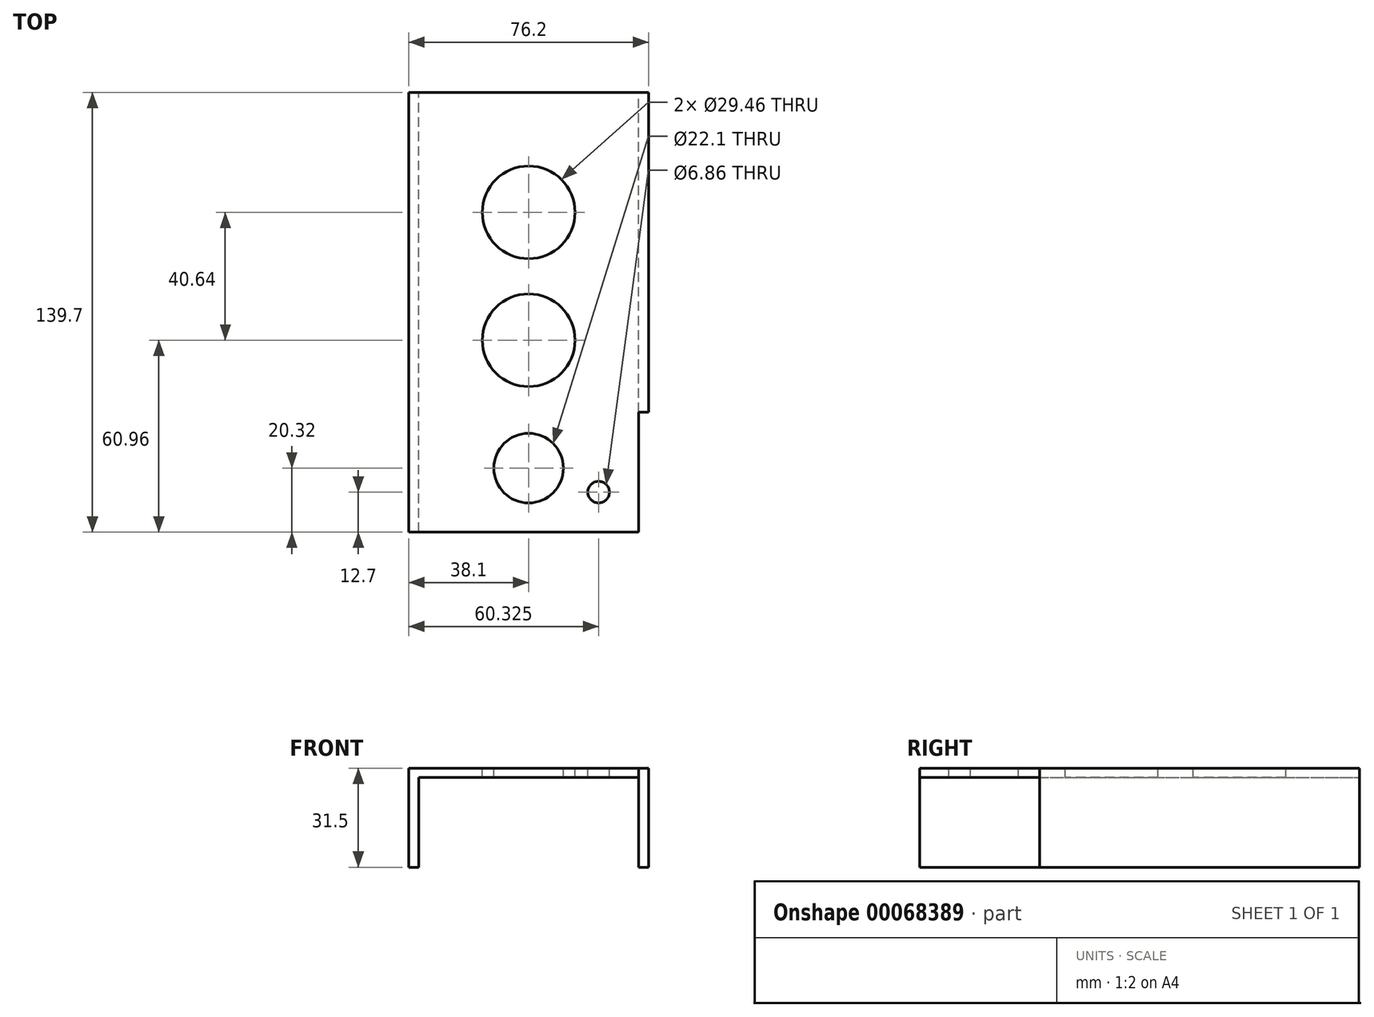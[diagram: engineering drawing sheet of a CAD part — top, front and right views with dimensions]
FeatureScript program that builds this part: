
annotation { "Feature Type Name" : "Feature", "Feature Type Description" : "" }
export const myFeature = defineFeature(function(context is Context, id is Id, definition is map)
    precondition{}
    {
        {
            var Q0;
            Q0=qCreatedBy(makeId("Top.planeOp"),FACE);
            var sketch = newSketch(context, id + "F0", { "sketchPlane" : qUnion([Q0])});
            skLineSegment(sketch, "E0.bottom", {"start": v(38.1, 69.85) * mm, "end": v(-38.1, 69.85) * mm});
            skLineSegment(sketch, "E0.top", {"start": v(38.1, -69.85) * mm, "end": v(-38.1, -69.85) * mm});
            skLineSegment(sketch, "E0.left", {"start": v(38.1, 69.85) * mm, "end": v(38.1, -69.85) * mm});
            skLineSegment(sketch, "E0.right", {"start": v(-38.1, 69.85) * mm, "end": v(-38.1, -69.85) * mm});
            skPoint(sketch, "E0.middle", {"position": v(0, 0) * mm});
            skSolve(sketch);
        }
        {
            var Q0;
            Q0 = qSketchRegion(id + "F0", true);
            extrude(context, id + "F1", {"entities" : qUnion([Q0]), "depth" : 4.76 * mm});
        }
        {
            var Q0;
            Q0=makeQuery(id+"F1.opExtrude","CAP_FACE",FACE,{"disambiguationData":[OSD([sQuery(id+"F0.wireOp",EDGE,"E0.bottom"),sQuery(id+"F0.wireOp",EDGE,"E0.top"),sQuery(id+"F0.wireOp",EDGE,"E0.left"),sQuery(id+"F0.wireOp",EDGE,"E0.right")])],"isStart":false});
            var sketch = newSketch(context, id + "F2", { "sketchPlane" : qUnion([Q0])});
            skLineSegment(sketch, "E1", {"start": v(0, -69.85) * mm, "end": v(34.92, -69.85) * mm, "construction": true});
            skLineSegment(sketch, "E2", {"start": v(0, -69.85) * mm, "end": v(-34.93, -69.85) * mm, "construction": true});
            skLineSegment(sketch, "E3.bottom", {"start": v(-34.93, -69.85) * mm, "end": v(-38.1, -69.85) * mm});
            skLineSegment(sketch, "E3.top", {"start": v(-34.93, 69.85) * mm, "end": v(-38.1, 69.85) * mm});
            skLineSegment(sketch, "E3.left", {"start": v(-34.93, -69.85) * mm, "end": v(-34.93, 69.85) * mm});
            skLineSegment(sketch, "E3.right", {"start": v(-38.1, -69.85) * mm, "end": v(-38.1, 69.85) * mm});
            skLineSegment(sketch, "E4.bottom", {"start": v(34.92, -69.85) * mm, "end": v(38.1, -69.85) * mm});
            skLineSegment(sketch, "E4.top", {"start": v(34.92, 69.85) * mm, "end": v(38.1, 69.85) * mm});
            skLineSegment(sketch, "E4.left", {"start": v(34.92, -69.85) * mm, "end": v(34.92, 69.85) * mm});
            skLineSegment(sketch, "E4.right", {"start": v(38.1, -69.85) * mm, "end": v(38.1, 69.85) * mm});
            skSolve(sketch);
        }
        {
            var Q0;
            Q0 = qSketchRegion(id + "F2", true);
            extrude(context, id + "F3", {"entities" : qUnion([Q0]), "operationType" : NewBodyOperationType.ADD, "depth" : 28.57 * mm});
        }
        {
            var Q0;
            Q0=makeQuery(id+"F3.opExtrude","CAP_FACE",FACE,{"disambiguationData":[OSD([sQuery(id+"F2.wireOp",EDGE,"E4.bottom"),sQuery(id+"F2.wireOp",EDGE,"E4.top"),sQuery(id+"F2.wireOp",EDGE,"E4.left"),sQuery(id+"F2.wireOp",EDGE,"E4.right")])],"isStart":false});
            var sketch = newSketch(context, id + "F4", { "sketchPlane" : qUnion([Q0])});
            skLineSegment(sketch, "E5.bottom", {"start": v(38.1, -69.85) * mm, "end": v(-38.1, -69.85) * mm});
            skLineSegment(sketch, "E5.top", {"start": v(38.1, 69.85) * mm, "end": v(-38.1, 69.85) * mm});
            skLineSegment(sketch, "E5.left", {"start": v(38.1, -69.85) * mm, "end": v(38.1, 69.85) * mm});
            skLineSegment(sketch, "E5.right", {"start": v(-38.1, -69.85) * mm, "end": v(-38.1, 69.85) * mm});
            skPoint(sketch, "E5.middle", {"position": v(0, 0) * mm});
            skSolve(sketch);
        }
        {
            var Q0;
            Q0 = qSketchRegion(id + "F4", true);
            extrude(context, id + "F5", {"entities" : qUnion([Q0]), "operationType" : NewBodyOperationType.ADD, "depth" : 2.92 * mm});
        }
        {
            var Q0;
            Q0=makeQuery(id+"F5.opExtrude","CAP_FACE",FACE,{"disambiguationData":[OSD([sQuery(id+"F4.wireOp",EDGE,"E5.bottom"),sQuery(id+"F4.wireOp",EDGE,"E5.top"),sQuery(id+"F4.wireOp",EDGE,"E5.left"),sQuery(id+"F4.wireOp",EDGE,"E5.right")])],"isStart":false});
            var sketch = newSketch(context, id + "F6", { "sketchPlane" : qUnion([Q0])});
            skLineSegment(sketch, "E6", {"start": v(0, 69.85) * mm, "end": v(0, 31.75) * mm, "construction": true});
            skPoint(sketch, "E6.endSnap0", {"position": v(0, 69.85) * mm});
            skCircle(sketch, "E7", {"center": v(0, 31.75) * mm, "radius": 14.73 * mm});
            skLineSegment(sketch, "E8", {"start": v(0, 31.75) * mm, "end": v(0, -8.9) * mm, "construction": true});
            skCircle(sketch, "E9", {"center": v(0, -8.9) * mm, "radius": 11.68 * mm});
            skLineSegment(sketch, "E10", {"start": v(0, -8.9) * mm, "end": v(0, -49.53) * mm, "construction": true});
            skCircle(sketch, "E11", {"center": v(0, -49.53) * mm, "radius": 11.05 * mm});
            skSolve(sketch);
        }
        {
            var Q0;
            Q0=makeQuery(id+"F6.imprint","IMPRINT",FACE,{"disambiguationData":[TD([[makeQuery(id+"F6.imprint","IMPRINT",EDGE,{"derivedFrom":sQuery(id+"F6.wireOp",EDGE,"E9")}),1.0]])]});
            var Q1;
            Q1=makeQuery(id+"F6.imprint","IMPRINT",FACE,{"disambiguationData":[TD([[makeQuery(id+"F6.imprint","IMPRINT",EDGE,{"derivedFrom":sQuery(id+"F6.wireOp",EDGE,"E11")}),1.0]])]});
            extrude(context, id + "F7", {"entities" : qUnion([Q0, Q1]), "operationType" : NewBodyOperationType.REMOVE, "oppositeDirection" : true, "depth" : 76.2 * mm});
        }
        {
            var Q0;
            Q0=makeQuery(id+"F6.imprint","IMPRINT",FACE,{"disambiguationData":[TD([[makeQuery(id+"F6.imprint","IMPRINT",EDGE,{"derivedFrom":sQuery(id+"F6.wireOp",EDGE,"E7")}),1.0]])]});
            extrude(context, id + "F8", {"entities" : qUnion([Q0]), "operationType" : NewBodyOperationType.REMOVE, "oppositeDirection" : true, "depth" : 25.4 * mm});
        }
        {
            var Q0;
            Q0=makeQuery(id+"F1.opExtrude","CAP_FACE",FACE,{"disambiguationData":[OSD([sQuery(id+"F0.wireOp",EDGE,"E0.bottom"),sQuery(id+"F0.wireOp",EDGE,"E0.top"),sQuery(id+"F0.wireOp",EDGE,"E0.left"),sQuery(id+"F0.wireOp",EDGE,"E0.right")])],"isStart":true});
            var sketch = newSketch(context, id + "F9", { "sketchPlane" : qUnion([Q0])});
            skLineSegment(sketch, "E12", {"start": v(0, -69.85) * mm, "end": v(0, -34.3) * mm, "construction": true});
            skPoint(sketch, "E12.endSnap0", {"position": v(0, -69.85) * mm});
            skCircle(sketch, "E13", {"center": v(0, -34.3) * mm, "radius": 11.43 * mm});
            skSolve(sketch);
        }
        {
            var Q0;
            Q0 = qSketchRegion(id + "F9", true);
            extrude(context, id + "F10", {"entities" : qUnion([Q0]), "operationType" : NewBodyOperationType.REMOVE, "oppositeDirection" : true, "depth" : 25.4 * mm});
        }
        {
            var Q0;
            Q0=makeQuery(id+"F1.opExtrude","CAP_FACE",FACE,{"disambiguationData":[OSD([sQuery(id+"F0.wireOp",EDGE,"E0.bottom"),sQuery(id+"F0.wireOp",EDGE,"E0.top"),sQuery(id+"F0.wireOp",EDGE,"E0.left"),sQuery(id+"F0.wireOp",EDGE,"E0.right")])],"isStart":true});
            var sketch = newSketch(context, id + "F11", { "sketchPlane" : qUnion([Q0])});
            skLineSegment(sketch, "E14.bottom", {"start": v(-38.1, -69.85) * mm, "end": v(38.1, -69.85) * mm});
            skLineSegment(sketch, "E14.top", {"start": v(-38.1, 69.85) * mm, "end": v(38.1, 69.85) * mm});
            skLineSegment(sketch, "E14.left", {"start": v(-38.1, -69.85) * mm, "end": v(-38.1, 69.85) * mm});
            skLineSegment(sketch, "E14.right", {"start": v(38.1, -69.85) * mm, "end": v(38.1, 69.85) * mm});
            skSolve(sketch);
        }
        {
            var Q0;
            Q0 = qSketchRegion(id + "F11", true);
            extrude(context, id + "F12", {"entities" : qUnion([Q0]), "operationType" : NewBodyOperationType.REMOVE, "oppositeDirection" : true, "depth" : 4.76 * mm});
        }
        {
            var Q0;
            Q0=makeQuery(id+"F5.opExtrude","CAP_FACE",FACE,{"disambiguationData":[OSD([sQuery(id+"F4.wireOp",EDGE,"E5.bottom"),sQuery(id+"F4.wireOp",EDGE,"E5.top"),sQuery(id+"F4.wireOp",EDGE,"E5.left"),sQuery(id+"F4.wireOp",EDGE,"E5.right")])],"isStart":false});
            var sketch = newSketch(context, id + "F13", { "sketchPlane" : qUnion([Q0])});
            skCircle(sketch, "E15", {"center": v(0, -8.9) * mm, "radius": 14.73 * mm});
            skSolve(sketch);
        }
        {
            var Q0;
            Q0 = qSketchRegion(id + "F13", true);
            extrude(context, id + "F14", {"entities" : qUnion([Q0]), "operationType" : NewBodyOperationType.REMOVE, "oppositeDirection" : true, "depth" : 25.4 * mm});
        }
        {
            var Q0;
            Q0=makeQuery(id+"F12.boolean.opBoolean","COPY",FACE,{"disambiguationData":[OD(1.0)],"derivedFrom":makeQuery(id+"F12.opExtrude","CAP_FACE",FACE,{"disambiguationData":[OSD([sQuery(id+"F11.wireOp",EDGE,"E14.bottom"),sQuery(id+"F11.wireOp",EDGE,"E14.top"),sQuery(id+"F11.wireOp",EDGE,"E14.left"),sQuery(id+"F11.wireOp",EDGE,"E14.right")])],"isStart":false})});
            var sketch = newSketch(context, id + "F15", { "sketchPlane" : qUnion([Q0])});
            skLineSegment(sketch, "E16.bottom", {"start": v(38.1, 69.85) * mm, "end": v(34.92, 69.85) * mm});
            skLineSegment(sketch, "E16.top", {"start": v(38.1, 31.75) * mm, "end": v(34.92, 31.75) * mm});
            skLineSegment(sketch, "E16.left", {"start": v(38.1, 69.85) * mm, "end": v(38.1, 31.75) * mm});
            skLineSegment(sketch, "E16.right", {"start": v(34.92, 69.85) * mm, "end": v(34.92, 31.75) * mm});
            skSolve(sketch);
        }
        {
            var Q0;
            Q0 = qSketchRegion(id + "F15", true);
            extrude(context, id + "F16", {"entities" : qUnion([Q0]), "operationType" : NewBodyOperationType.REMOVE, "oppositeDirection" : true, "depth" : 49.04 * mm});
        }
        {
            var Q0;
            Q0=makeQuery(id+"F5.opExtrude","CAP_FACE",FACE,{"disambiguationData":[OSD([sQuery(id+"F4.wireOp",EDGE,"E5.bottom"),sQuery(id+"F4.wireOp",EDGE,"E5.top"),sQuery(id+"F4.wireOp",EDGE,"E5.left"),sQuery(id+"F4.wireOp",EDGE,"E5.right")])],"isStart":false});
            var sketch = newSketch(context, id + "F17", { "sketchPlane" : qUnion([Q0])});
            skLineSegment(sketch, "E17.bottom", {"start": v(34.92, -69.85) * mm, "end": v(22.22, -69.85) * mm, "construction": true});
            skLineSegment(sketch, "E17.top", {"start": v(34.92, -57.15) * mm, "end": v(22.22, -57.15) * mm, "construction": true});
            skLineSegment(sketch, "E17.left", {"start": v(34.92, -69.85) * mm, "end": v(34.92, -57.15) * mm, "construction": true});
            skLineSegment(sketch, "E17.right", {"start": v(22.22, -69.85) * mm, "end": v(22.22, -57.15) * mm, "construction": true});
            skLineSegment(sketch, "E18", {"start": v(22.22, -57.15) * mm, "end": v(-3.18, -57.15) * mm, "construction": true});
            skCircle(sketch, "E19", {"center": v(22.22, -57.15) * mm, "radius": 3.43 * mm});
            skSolve(sketch);
        }
        {
            var Q0;
            Q0 = qSketchRegion(id + "F17", true);
            extrude(context, id + "F18", {"entities" : qUnion([Q0]), "operationType" : NewBodyOperationType.REMOVE, "oppositeDirection" : true, "depth" : 25.4 * mm});
        }
    });
